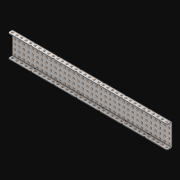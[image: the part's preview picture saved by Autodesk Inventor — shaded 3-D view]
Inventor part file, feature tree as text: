
AUTODESK INVENTOR PART (.ipt)
format: ipt  version: 2021 (Build 250183000, 183)  size: 3,905,536 bytes
history: native  units: in
note: dims shown in document units (in); Inventor stores cm internally (conversion verified against a paired STEP export)
features: other x245, extrude x245, thicken_offset x3, pattern_linear x3, sketch x3, imported_body x1
ambient origin geometry x8: Origin, YZ Plane, XZ Plane, XY Plane, X Axis, Y Axis, Z Axis, Center Point
bodies: Solid1 (feature_tree)
feature tree (500):
  thicken_offset  "Thicken1"
  thicken_offset  "Thicken2"
  thicken_offset  "Thicken3"
  pattern_linear  "Rectangular Pattern1"  Spacing1=0.001in  [1 undecoded]
  pattern_linear  "Rectangular Pattern2"  Spacing1=0.001in  [1 undecoded]
  pattern_linear  "Rectangular Pattern3"  Spacing1=0.001in  [1 undecoded]
  sketch  "Sketch1"  dims[d0=0.001in]
  other  "Srf1"
  sketch  "Sketch2"  dims[d1=0.001in]
  other  "Srf2"
  sketch  "Sketch3"  dims[d2=0.001in d3=0.001in d4=0.001in d5=0.001in d6=0.182in d7=0.063in d8=0.0in d9=0.182in d10=0.063in d11=0.0in d12=0.182in d13=0.063in d14=0.0in d17=0.5in d18=13.7795in d20=0.5in d21=13.7795in d23=0.5in d24=1.9685in d26=0.5in]
  other  "Srf3"
  other  "Srf4"
  other  "Srf5"
  other  "Srf6"
  other  "Srf7"
  other  "Srf8"
  other  "Srf9"
  other  "Srf10"
  other  "Srf11"
  other  "Srf12"
  other  "Srf13"
  other  "Srf14"
  other  "Srf15"
  other  "Srf16"
  other  "Srf17"
  other  "Srf18"
  other  "Srf19"
  other  "Srf20"
  other  "Srf21"
  other  "Srf22"
  other  "Srf23"
  other  "Srf24"
  other  "Srf25"
  other  "Srf26"
  other  "Srf27"
  other  "Srf28"
  other  "Srf29"
  other  "Srf30"
  other  "Srf31"
  other  "Srf32"
  other  "Srf33"
  other  "Srf34"
  other  "Srf35"
  other  "Srf36"
  other  "Srf37"
  other  "Srf38"
  other  "Srf39"
  other  "Srf40"
  other  "Srf41"
  other  "Srf42"
  other  "Srf43"
  other  "Srf44"
  other  "Srf45"
  other  "Srf46"
  other  "Srf47"
  other  "Srf48"
  other  "Srf49"
  other  "Srf50"
  other  "Srf51"
  other  "Srf52"
  other  "Srf53"
  other  "Srf54"
  other  "Srf55"
  other  "Srf56"
  other  "Srf57"
  other  "Srf58"
  other  "Srf59"
  other  "Srf60"
  other  "Srf61"
  other  "Srf62"
  other  "Srf63"
  other  "Srf64"
  other  "Srf65"
  other  "Srf66"
  other  "Srf67"
  other  "Srf68"
  other  "Srf69"
  other  "Srf70"
  other  "Srf71"
  other  "Srf72"
  other  "Srf73"
  other  "Srf74"
  other  "Srf75"
  other  "Srf76"
  other  "Srf77"
  other  "Srf78"
  other  "Srf79"
  other  "Srf80"
  other  "Srf81"
  other  "Srf82"
  other  "Srf83"
  other  "Srf84"
  other  "Srf85"
  other  "Srf86"
  other  "Srf87"
  other  "Srf88"
  other  "Srf89"
  other  "Srf90"
  other  "Srf91"
  other  "Srf92"
  other  "Srf93"
  other  "Srf94"
  other  "Srf95"
  other  "Srf96"
  other  "Srf97"
  other  "Srf98"
  other  "Srf99"
  other  "Srf100"
  other  "Srf101"
  other  "Srf102"
  other  "Srf103"
  other  "Srf104"
  other  "Srf105"
  other  "Srf106"
  other  "Srf107"
  other  "Srf108"
  other  "Srf109"
  other  "Srf110"
  other  "Srf111"
  other  "Srf112"
  other  "Srf113"
  other  "Srf114"
  other  "Srf115"
  other  "Srf116"
  other  "Srf117"
  other  "Srf118"
  other  "Srf119"
  other  "Srf120"
  other  "Srf121"
  other  "Srf122"
  other  "Srf123"
  other  "Srf124"
  other  "Srf125"
  other  "Srf126"
  other  "Srf127"
  other  "Srf128"
  other  "Srf129"
  other  "Srf130"
  other  "Srf131"
  other  "Srf132"
  other  "Srf133"
  other  "Srf134"
  other  "Srf135"
  other  "Srf136"
  other  "Srf137"
  other  "Srf138"
  other  "Srf139"
  other  "Srf140"
  other  "Srf141"
  other  "Srf142"
  other  "Srf143"
  other  "Srf144"
  other  "Srf145"
  other  "Srf146"
  other  "Srf147"
  other  "Srf148"
  other  "Srf149"
  other  "Srf150"
  other  "Srf151"
  other  "Srf152"
  other  "Srf153"
  other  "Srf154"
  other  "Srf155"
  other  "Srf156"
  other  "Srf157"
  other  "Srf158"
  other  "Srf159"
  other  "Srf160"
  other  "Srf161"
  other  "Srf162"
  other  "Srf163"
  other  "Srf164"
  other  "Srf165"
  other  "Srf166"
  other  "Srf167"
  other  "Srf168"
  other  "Srf169"
  other  "Srf170"
  other  "Srf171"
  other  "Srf172"
  other  "Srf173"
  other  "Srf174"
  other  "Srf175"
  other  "Srf176"
  other  "Srf177"
  other  "Srf178"
  other  "Srf179"
  other  "Srf180"
  other  "Srf181"
  other  "Srf182"
  other  "Srf183"
  other  "Srf184"
  other  "Srf185"
  other  "Srf186"
  other  "Srf187"
  other  "Srf188"
  other  "Srf189"
  other  "Srf190"
  other  "Srf191"
  other  "Srf192"
  other  "Srf193"
  other  "Srf194"
  other  "Srf195"
  other  "Srf196"
  other  "Srf197"
  other  "Srf198"
  other  "Srf199"
  other  "Srf200"
  other  "Srf201"
  other  "Srf202"
  other  "Srf203"
  other  "Srf204"
  other  "Srf205"
  other  "Srf206"
  other  "Srf207"
  other  "Srf208"
  other  "Srf209"
  other  "Srf210"
  other  "Srf211"
  other  "Srf212"
  other  "Srf213"
  other  "Srf214"
  other  "Srf215"
  other  "Srf216"
  other  "Srf217"
  other  "Srf218"
  other  "Srf219"
  other  "Srf220"
  other  "Srf221"
  other  "Srf222"
  other  "Srf223"
  other  "Srf224"
  other  "Srf225"
  other  "Srf226"
  other  "Srf227"
  other  "Srf228"
  other  "Srf229"
  other  "Srf230"
  other  "Srf231"
  other  "Srf232"
  other  "Srf233"
  other  "Srf234"
  other  "Srf235"
  other  "Srf236"
  other  "Srf237"
  other  "Srf238"
  other  "Srf239"
  other  "Srf240"
  other  "Srf241"
  other  "Srf242"
  other  "Srf243"
  other  "Srf244"
  other  "Srf245"
  imported_body  "Imported1"
  extrude  "ExtrusionSrf1"  Depth=0.5in
  extrude  "ExtrusionSrf2"  Depth=0.5in TaperAngle=0.0deg
  extrude  "ExtrusionSrf3"  Depth=0.5in
  extrude  "ExtrusionSrf4"  Depth=0.5in TaperAngle=0.0deg
  extrude  "ExtrusionSrf5"  Depth=0.5in
  extrude  "ExtrusionSrf6"  Depth=0.5in TaperAngle=0.0deg
  extrude  "ExtrusionSrf7"  Depth=0.5in
  extrude  "ExtrusionSrf8"  Depth=0.5in
  extrude  "ExtrusionSrf9"  Depth=0.5in
  extrude  "ExtrusionSrf10"  Depth=0.5in
  extrude  "ExtrusionSrf11"  Depth=0.5in
  extrude  "ExtrusionSrf12"  Depth=0.5in
  extrude  "ExtrusionSrf13"  [1 undecoded]
  extrude  "ExtrusionSrf14"  [1 undecoded]
  extrude  "ExtrusionSrf15"  [1 undecoded]
  extrude  "ExtrusionSrf16"  [1 undecoded]
  extrude  "ExtrusionSrf17"  [1 undecoded]
  extrude  "ExtrusionSrf18"  [1 undecoded]
  extrude  "ExtrusionSrf19"  [1 undecoded]
  extrude  "ExtrusionSrf20"  [1 undecoded]
  extrude  "ExtrusionSrf21"  [1 undecoded]
  extrude  "ExtrusionSrf22"  [1 undecoded]
  extrude  "ExtrusionSrf23"  [1 undecoded]
  extrude  "ExtrusionSrf24"  [1 undecoded]
  extrude  "ExtrusionSrf25"  [1 undecoded]
  extrude  "ExtrusionSrf26"  [1 undecoded]
  extrude  "ExtrusionSrf27"  [1 undecoded]
  extrude  "ExtrusionSrf28"  [1 undecoded]
  extrude  "ExtrusionSrf29"  [1 undecoded]
  extrude  "ExtrusionSrf30"  [1 undecoded]
  extrude  "ExtrusionSrf31"  [1 undecoded]
  extrude  "ExtrusionSrf32"  [1 undecoded]
  extrude  "ExtrusionSrf33"  [1 undecoded]
  extrude  "ExtrusionSrf34"  [1 undecoded]
  extrude  "ExtrusionSrf35"  [1 undecoded]
  extrude  "ExtrusionSrf36"  [1 undecoded]
  extrude  "ExtrusionSrf37"  [1 undecoded]
  extrude  "ExtrusionSrf38"  [1 undecoded]
  extrude  "ExtrusionSrf39"  [1 undecoded]
  extrude  "ExtrusionSrf40"  [1 undecoded]
  extrude  "ExtrusionSrf41"  [1 undecoded]
  extrude  "ExtrusionSrf42"  [1 undecoded]
  extrude  "ExtrusionSrf43"  [1 undecoded]
  extrude  "ExtrusionSrf44"  [1 undecoded]
  extrude  "ExtrusionSrf45"  [1 undecoded]
  extrude  "ExtrusionSrf46"  [1 undecoded]
  extrude  "ExtrusionSrf47"  [1 undecoded]
  extrude  "ExtrusionSrf48"  [1 undecoded]
  extrude  "ExtrusionSrf49"  [1 undecoded]
  extrude  "ExtrusionSrf50"  [1 undecoded]
  extrude  "ExtrusionSrf51"  [1 undecoded]
  extrude  "ExtrusionSrf52"  [1 undecoded]
  extrude  "ExtrusionSrf53"  [1 undecoded]
  extrude  "ExtrusionSrf54"  [1 undecoded]
  extrude  "ExtrusionSrf55"  [1 undecoded]
  extrude  "ExtrusionSrf56"  [1 undecoded]
  extrude  "ExtrusionSrf57"  [1 undecoded]
  extrude  "ExtrusionSrf58"  [1 undecoded]
  extrude  "ExtrusionSrf59"  [1 undecoded]
  extrude  "ExtrusionSrf60"  [1 undecoded]
  extrude  "ExtrusionSrf61"  [1 undecoded]
  extrude  "ExtrusionSrf62"  [1 undecoded]
  extrude  "ExtrusionSrf63"  [1 undecoded]
  extrude  "ExtrusionSrf64"  [1 undecoded]
  extrude  "ExtrusionSrf65"  [1 undecoded]
  extrude  "ExtrusionSrf66"  [1 undecoded]
  extrude  "ExtrusionSrf67"  [1 undecoded]
  extrude  "ExtrusionSrf68"  [1 undecoded]
  extrude  "ExtrusionSrf69"  [1 undecoded]
  extrude  "ExtrusionSrf70"  [1 undecoded]
  extrude  "ExtrusionSrf71"  [1 undecoded]
  extrude  "ExtrusionSrf72"  [1 undecoded]
  extrude  "ExtrusionSrf73"  [1 undecoded]
  extrude  "ExtrusionSrf74"  [1 undecoded]
  extrude  "ExtrusionSrf75"  [1 undecoded]
  extrude  "ExtrusionSrf76"  [1 undecoded]
  extrude  "ExtrusionSrf77"  [1 undecoded]
  extrude  "ExtrusionSrf78"  [1 undecoded]
  extrude  "ExtrusionSrf79"  [1 undecoded]
  extrude  "ExtrusionSrf80"  [1 undecoded]
  extrude  "ExtrusionSrf81"  [1 undecoded]
  extrude  "ExtrusionSrf82"  [1 undecoded]
  extrude  "ExtrusionSrf83"  [1 undecoded]
  extrude  "ExtrusionSrf84"  [1 undecoded]
  extrude  "ExtrusionSrf85"  [1 undecoded]
  extrude  "ExtrusionSrf86"  [1 undecoded]
  extrude  "ExtrusionSrf87"  [1 undecoded]
  extrude  "ExtrusionSrf88"  [1 undecoded]
  extrude  "ExtrusionSrf89"  [1 undecoded]
  extrude  "ExtrusionSrf90"  [1 undecoded]
  extrude  "ExtrusionSrf91"  [1 undecoded]
  extrude  "ExtrusionSrf92"  [1 undecoded]
  extrude  "ExtrusionSrf93"  [1 undecoded]
  extrude  "ExtrusionSrf94"  [1 undecoded]
  extrude  "ExtrusionSrf95"  [1 undecoded]
  extrude  "ExtrusionSrf96"  [1 undecoded]
  extrude  "ExtrusionSrf97"  [1 undecoded]
  extrude  "ExtrusionSrf98"  [1 undecoded]
  extrude  "ExtrusionSrf99"  [1 undecoded]
  extrude  "ExtrusionSrf100"  [1 undecoded]
  extrude  "ExtrusionSrf101"  [1 undecoded]
  extrude  "ExtrusionSrf102"  [1 undecoded]
  extrude  "ExtrusionSrf103"  [1 undecoded]
  extrude  "ExtrusionSrf104"  [1 undecoded]
  extrude  "ExtrusionSrf105"  [1 undecoded]
  extrude  "ExtrusionSrf106"  [1 undecoded]
  extrude  "ExtrusionSrf107"  [1 undecoded]
  extrude  "ExtrusionSrf108"  [1 undecoded]
  extrude  "ExtrusionSrf109"  [1 undecoded]
  extrude  "ExtrusionSrf110"  [1 undecoded]
  extrude  "ExtrusionSrf111"  [1 undecoded]
  extrude  "ExtrusionSrf112"  [1 undecoded]
  extrude  "ExtrusionSrf113"  [1 undecoded]
  extrude  "ExtrusionSrf114"  [1 undecoded]
  extrude  "ExtrusionSrf115"  [1 undecoded]
  extrude  "ExtrusionSrf116"  [1 undecoded]
  extrude  "ExtrusionSrf117"  [1 undecoded]
  extrude  "ExtrusionSrf118"  [1 undecoded]
  extrude  "ExtrusionSrf119"  [1 undecoded]
  extrude  "ExtrusionSrf120"  [1 undecoded]
  extrude  "ExtrusionSrf121"  [1 undecoded]
  extrude  "ExtrusionSrf122"  [1 undecoded]
  extrude  "ExtrusionSrf123"  [1 undecoded]
  extrude  "ExtrusionSrf124"  [1 undecoded]
  extrude  "ExtrusionSrf125"  [1 undecoded]
  extrude  "ExtrusionSrf126"  [1 undecoded]
  extrude  "ExtrusionSrf127"  [1 undecoded]
  extrude  "ExtrusionSrf128"  [1 undecoded]
  extrude  "ExtrusionSrf129"  [1 undecoded]
  extrude  "ExtrusionSrf130"  [1 undecoded]
  extrude  "ExtrusionSrf131"  [1 undecoded]
  extrude  "ExtrusionSrf132"  [1 undecoded]
  extrude  "ExtrusionSrf133"  [1 undecoded]
  extrude  "ExtrusionSrf134"  [1 undecoded]
  extrude  "ExtrusionSrf135"  [1 undecoded]
  extrude  "ExtrusionSrf136"  [1 undecoded]
  extrude  "ExtrusionSrf137"  [1 undecoded]
  extrude  "ExtrusionSrf138"  [1 undecoded]
  extrude  "ExtrusionSrf139"  [1 undecoded]
  extrude  "ExtrusionSrf140"  [1 undecoded]
  extrude  "ExtrusionSrf141"  [1 undecoded]
  extrude  "ExtrusionSrf142"  [1 undecoded]
  extrude  "ExtrusionSrf143"  [1 undecoded]
  extrude  "ExtrusionSrf144"  [1 undecoded]
  extrude  "ExtrusionSrf145"  [1 undecoded]
  extrude  "ExtrusionSrf146"  [1 undecoded]
  extrude  "ExtrusionSrf147"  [1 undecoded]
  extrude  "ExtrusionSrf148"  [1 undecoded]
  extrude  "ExtrusionSrf149"  [1 undecoded]
  extrude  "ExtrusionSrf150"  [1 undecoded]
  extrude  "ExtrusionSrf151"  [1 undecoded]
  extrude  "ExtrusionSrf152"  [1 undecoded]
  extrude  "ExtrusionSrf153"  [1 undecoded]
  extrude  "ExtrusionSrf154"  [1 undecoded]
  extrude  "ExtrusionSrf155"  [1 undecoded]
  extrude  "ExtrusionSrf156"  [1 undecoded]
  extrude  "ExtrusionSrf157"  [1 undecoded]
  extrude  "ExtrusionSrf158"  [1 undecoded]
  extrude  "ExtrusionSrf159"  [1 undecoded]
  extrude  "ExtrusionSrf160"  [1 undecoded]
  extrude  "ExtrusionSrf161"  [1 undecoded]
  extrude  "ExtrusionSrf162"  [1 undecoded]
  extrude  "ExtrusionSrf163"  [1 undecoded]
  extrude  "ExtrusionSrf164"  [1 undecoded]
  extrude  "ExtrusionSrf165"  [1 undecoded]
  extrude  "ExtrusionSrf166"  [1 undecoded]
  extrude  "ExtrusionSrf167"  [1 undecoded]
  extrude  "ExtrusionSrf168"  [1 undecoded]
  extrude  "ExtrusionSrf169"  [1 undecoded]
  extrude  "ExtrusionSrf170"  [1 undecoded]
  extrude  "ExtrusionSrf171"  [1 undecoded]
  extrude  "ExtrusionSrf172"  [1 undecoded]
  extrude  "ExtrusionSrf173"  [1 undecoded]
  extrude  "ExtrusionSrf174"  [1 undecoded]
  extrude  "ExtrusionSrf175"  [1 undecoded]
  extrude  "ExtrusionSrf176"  [1 undecoded]
  extrude  "ExtrusionSrf177"  [1 undecoded]
  extrude  "ExtrusionSrf178"  [1 undecoded]
  extrude  "ExtrusionSrf179"  [1 undecoded]
  extrude  "ExtrusionSrf180"  [1 undecoded]
  extrude  "ExtrusionSrf181"  [1 undecoded]
  extrude  "ExtrusionSrf182"  [1 undecoded]
  extrude  "ExtrusionSrf183"  [1 undecoded]
  extrude  "ExtrusionSrf184"  [1 undecoded]
  extrude  "ExtrusionSrf185"  [1 undecoded]
  extrude  "ExtrusionSrf186"  [1 undecoded]
  extrude  "ExtrusionSrf187"  [1 undecoded]
  extrude  "ExtrusionSrf188"  [1 undecoded]
  extrude  "ExtrusionSrf189"  [1 undecoded]
  extrude  "ExtrusionSrf190"  [1 undecoded]
  extrude  "ExtrusionSrf191"  [1 undecoded]
  extrude  "ExtrusionSrf192"  [1 undecoded]
  extrude  "ExtrusionSrf193"  [1 undecoded]
  extrude  "ExtrusionSrf194"  [1 undecoded]
  extrude  "ExtrusionSrf195"  [1 undecoded]
  extrude  "ExtrusionSrf196"  [1 undecoded]
  extrude  "ExtrusionSrf197"  [1 undecoded]
  extrude  "ExtrusionSrf198"  [1 undecoded]
  extrude  "ExtrusionSrf199"  [1 undecoded]
  extrude  "ExtrusionSrf200"  [1 undecoded]
  extrude  "ExtrusionSrf201"  [1 undecoded]
  extrude  "ExtrusionSrf202"  [1 undecoded]
  extrude  "ExtrusionSrf203"  [1 undecoded]
  extrude  "ExtrusionSrf204"  [1 undecoded]
  extrude  "ExtrusionSrf205"  [1 undecoded]
  extrude  "ExtrusionSrf206"  [1 undecoded]
  extrude  "ExtrusionSrf207"  [1 undecoded]
  extrude  "ExtrusionSrf208"  [1 undecoded]
  extrude  "ExtrusionSrf209"  [1 undecoded]
  extrude  "ExtrusionSrf210"  [1 undecoded]
  extrude  "ExtrusionSrf211"  [1 undecoded]
  extrude  "ExtrusionSrf212"  [1 undecoded]
  extrude  "ExtrusionSrf213"  [1 undecoded]
  extrude  "ExtrusionSrf214"  [1 undecoded]
  extrude  "ExtrusionSrf215"  [1 undecoded]
  extrude  "ExtrusionSrf216"  [1 undecoded]
  extrude  "ExtrusionSrf217"  [1 undecoded]
  extrude  "ExtrusionSrf218"  [1 undecoded]
  extrude  "ExtrusionSrf219"  [1 undecoded]
  extrude  "ExtrusionSrf220"  [1 undecoded]
  extrude  "ExtrusionSrf221"  [1 undecoded]
  extrude  "ExtrusionSrf222"  [1 undecoded]
  extrude  "ExtrusionSrf223"  [1 undecoded]
  extrude  "ExtrusionSrf224"  [1 undecoded]
  extrude  "ExtrusionSrf225"  [1 undecoded]
  extrude  "ExtrusionSrf226"  [1 undecoded]
  extrude  "ExtrusionSrf227"  [1 undecoded]
  extrude  "ExtrusionSrf228"  [1 undecoded]
  extrude  "ExtrusionSrf229"  [1 undecoded]
  extrude  "ExtrusionSrf230"  [1 undecoded]
  extrude  "ExtrusionSrf231"  [1 undecoded]
  extrude  "ExtrusionSrf232"  [1 undecoded]
  extrude  "ExtrusionSrf233"  [1 undecoded]
  extrude  "ExtrusionSrf234"  [1 undecoded]
  extrude  "ExtrusionSrf235"  [1 undecoded]
  extrude  "ExtrusionSrf236"  [1 undecoded]
  extrude  "ExtrusionSrf237"  [1 undecoded]
  extrude  "ExtrusionSrf238"  [1 undecoded]
  extrude  "ExtrusionSrf239"  [1 undecoded]
  extrude  "ExtrusionSrf240"  [1 undecoded]
  extrude  "ExtrusionSrf241"  [1 undecoded]
  extrude  "ExtrusionSrf242"  [1 undecoded]
  extrude  "ExtrusionSrf243"  [1 undecoded]
  extrude  "ExtrusionSrf244"  [1 undecoded]
  extrude  "ExtrusionSrf245"  [1 undecoded]
note: 236 required parameter values undecoded (feature->parameter linkage not recoverable at this tier; creation-order binding heuristic only, values carry confidence <= 0.55)
